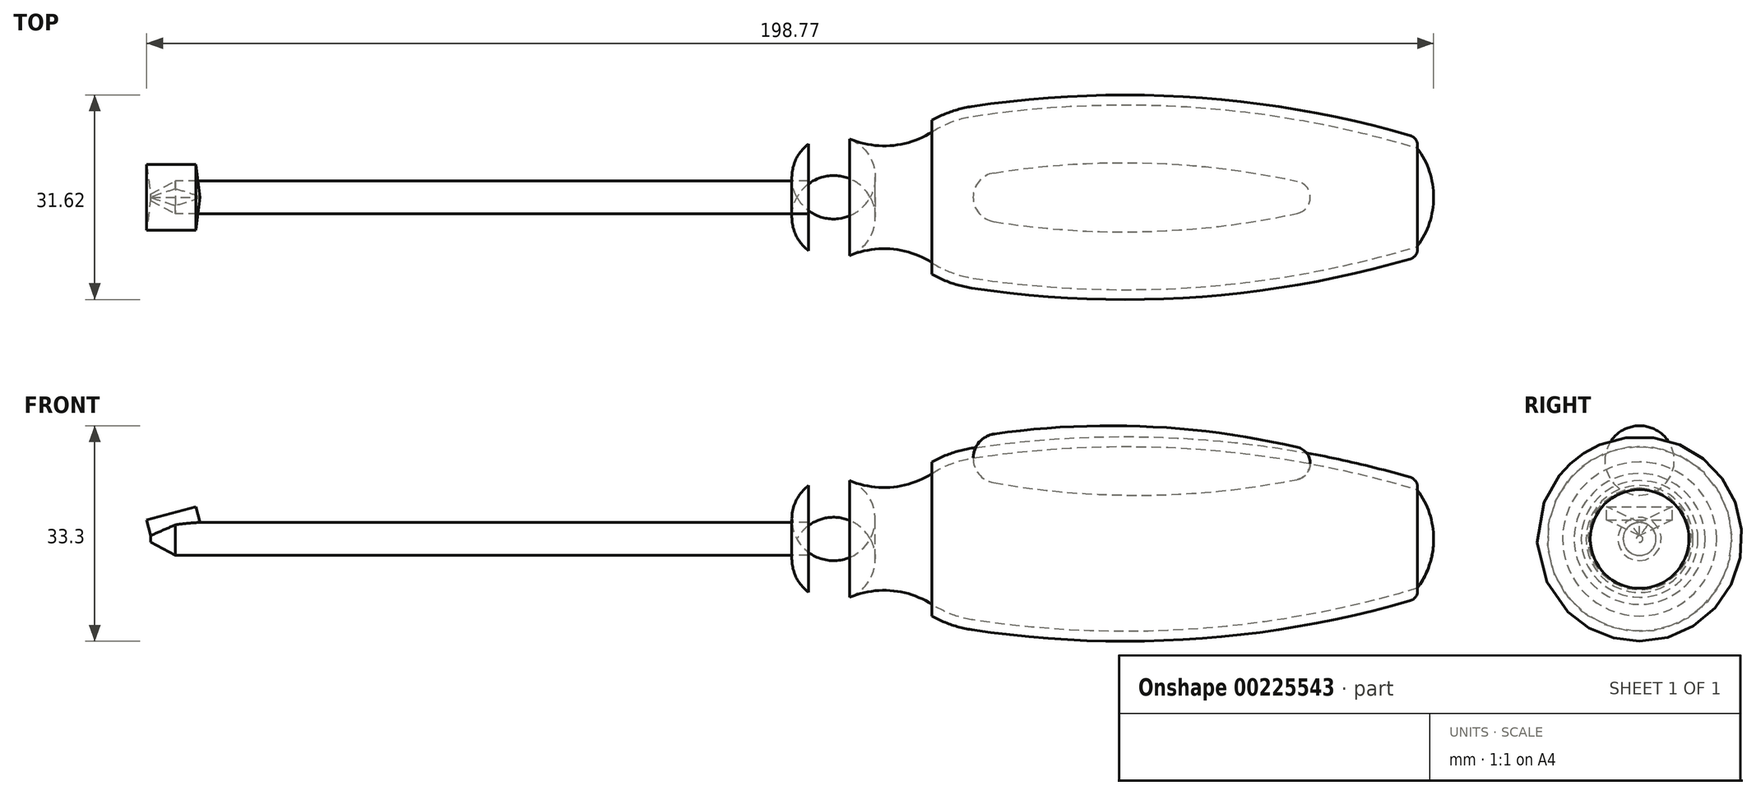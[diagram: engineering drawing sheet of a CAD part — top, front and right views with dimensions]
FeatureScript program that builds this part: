
annotation { "Feature Type Name" : "Feature", "Feature Type Description" : "" }
export const myFeature = defineFeature(function(context is Context, id is Id, definition is map)
    precondition{}
    {
        {
            var Q0;
            Q0=qCreatedBy(makeId("Front.planeOp"),FACE);
            var sketch = newSketch(context, id + "F0", { "sketchPlane" : qUnion([Q0])});
            skLineSegment(sketch, "E0", {"start": v(-101.6, 0) * mm, "end": v(96.52, 0) * mm});
            skLineSegment(sketch, "E1", {"start": v(96.52, 0) * mm, "end": v(117.55, 0) * mm, "construction": true});
            skLineSegment(sketch, "E2", {"start": v(50.8, 2.54) * mm, "end": v(-97.8, 2.54) * mm});
            skLineSegment(sketch, "E3", {"start": v(-101.6, 0.5) * mm, "end": v(-101.6, 0) * mm});
            skLineSegment(sketch, "E4", {"start": v(0, 2.54) * mm, "end": v(0, 8.25) * mm});
            skArc(sketch, "E5", {"start": v(6.35, 9.02) * mm, "mid": v(3.07, 9.48) * mm, "end": v(0, 8.25) * mm});
            skArc(sketch, "E6", {"start": v(6.35, 9.02) * mm, "mid": v(12.84, 7.99) * mm, "end": v(19.05, 10.11) * mm});
            skArc(sketch, "E7", {"start": v(25.4, 12.52) * mm, "mid": v(22.1, 11.65) * mm, "end": v(19.05, 10.11) * mm});
            skArc(sketch, "E8", {"start": v(93.98, 7.62) * mm, "mid": v(59.96, 13.9) * mm, "end": v(25.4, 12.52) * mm});
            skArc(sketch, "E9", {"start": v(96.52, 0) * mm, "mid": v(95.87, 4.02) * mm, "end": v(93.98, 7.62) * mm});
            skArc(sketch, "E10.0", {"start": v(25.17, 14.02) * mm, "mid": v(22.01, 13.24) * mm, "end": v(19.05, 11.9) * mm});
            skArc(sketch, "E10.1", {"start": v(92.95, 9.52) * mm, "mid": v(59.3, 15.46) * mm, "end": v(25.17, 14.02) * mm});
            skLineSegment(sketch, "E11", {"start": v(19.05, 11.9) * mm, "end": v(19.05, 10.11) * mm});
            skArc(sketch, "E12", {"start": v(93.98, 7.62) * mm, "mid": v(93.86, 8.78) * mm, "end": v(92.95, 9.52) * mm});
            skPoint(sketch, "E13.orphan", {"position": v(0, 0) * mm});
            skLineSegment(sketch, "E14", {"start": v(50.8, 2.54) * mm, "end": v(50.8, 0) * mm});
            skLineSegment(sketch, "E15", {"start": v(-101.6, 0.5) * mm, "end": v(-97.8, 2.54) * mm});
            skPoint(sketch, "E16.orphan", {"position": v(-101.6, 2.54) * mm});
            skSolve(sketch);
        }
        {
            var Q0;
            Q0=qCreatedBy(makeId("Front.planeOp"),FACE);
            var sketch = newSketch(context, id + "F1", { "sketchPlane" : qUnion([Q0])});
            skLineSegment(sketch, "E17", {"start": v(25.4, 12.52) * mm, "end": v(77.47, 11.64) * mm});
            skArc(sketch, "E18", {"start": v(28.67, 16.22) * mm, "mid": v(26.35, 14.97) * mm, "end": v(25.4, 12.52) * mm});
            skArc(sketch, "E19", {"start": v(77.47, 11.64) * mm, "mid": v(76.93, 13.25) * mm, "end": v(75.5, 14.16) * mm});
            skArc(sketch, "E20", {"start": v(75.5, 14.16) * mm, "mid": v(52.19, 17.37) * mm, "end": v(28.67, 16.22) * mm});
            skSolve(sketch);
        }
        {
            var Q0;
            Q0=qCreatedBy(makeId("Front.planeOp"),FACE);
            var sketch = newSketch(context, id + "F2", { "sketchPlane" : qUnion([Q0])});
            skLineSegment(sketch, "E21", {"start": v(-101.6, 0.5) * mm, "end": v(-93.98, 2.54) * mm});
            skSolve(sketch);
        }
        {
            var Q0;
            Q0=sQuery(id+"F2.wireOp",VERTEX,"E21.start");
            var Q1;
            Q1=sQuery(id+"F2.wireOp",EDGE,"E21");
            cPlane(context, id + "F3", {"entities" : qUnion([Q0, Q1]), "cplaneType" : CPlaneType.LINE_POINT, "offset" : 25.4 * mm, "width" : 152.4 * mm, "height" : 152.4 * mm});
        }
        {
            var Q0;
            Q0=qCreatedBy(id+"F3.planeOp",FACE);
            var sketch = newSketch(context, id + "F4", { "sketchPlane" : qUnion([Q0])});
            skLineSegment(sketch, "E22", {"start": v(5.08, 29.2) * mm, "end": v(0, 26.67) * mm});
            skLineSegment(sketch, "E23", {"start": v(0, 26.67) * mm, "end": v(-5.08, 29.2) * mm});
            skLineSegment(sketch, "E24", {"start": v(-5.08, 29.2) * mm, "end": v(5.08, 29.2) * mm});
            skLineSegment(sketch, "E25", {"start": v(0, 29.2) * mm, "end": v(0, 26.67) * mm, "construction": true});
            skSolve(sketch);
        }
        {
            var Q0;
            {var subQ0=sQuery(id+"F0.wireOp",EDGE,"E3");Q0=makeQuery(id+"F0.imprint","IMPRINT",FACE,{"disambiguationData":[TD([[makeQuery(id+"F0.imprint","IMPRINT",EDGE,{"derivedFrom":subQ0}),1.0]])]});}
            var Q1;
            {var subQ0=sQuery(id+"F0.wireOp",EDGE,"E4");Q1=makeQuery(id+"F0.imprint","IMPRINT",FACE,{"disambiguationData":[TD([[makeQuery(id+"F0.imprint","IMPRINT",EDGE,{"derivedFrom":subQ0}),-1.0]])]});}
            var Q2;
            Q2=sQuery(id+"F0.wireOp",EDGE,"E1");
            revolve(context, id + "F5", {"entities" : qUnion([Q0, Q1]), "axis" : qUnion([Q2]), "revolveType" : RevolveType.FULL});
        }
        {
            var Q0;
            Q0=makeQuery(id+"F4.imprint","IMPRINT",FACE,{"disambiguationData":[TD([[makeQuery(id+"F4.imprint","IMPRINT",EDGE,{"derivedFrom":sQuery(id+"F4.wireOp",EDGE,"E22")}),-1.0]])]});
            var Q1;
            Q1=sQuery(id+"F2.wireOp",EDGE,"E21");
            sweep(context, id + "F6", {"operationType" : NewBodyOperationType.REMOVE, "profiles" : qUnion([Q0]), "path" : qUnion([Q1])});
        }
        {
            var Q0;
            Q0=makeQuery(id+"F1.imprint","IMPRINT",FACE,{"disambiguationData":[TD([[makeQuery(id+"F1.imprint","IMPRINT",EDGE,{"derivedFrom":sQuery(id+"F1.wireOp",EDGE,"E17")}),1.0]])]});
            var Q1;
            Q1=sQuery(id+"F1.wireOp",EDGE,"E17");
            revolve(context, id + "F7", {"entities" : qUnion([Q0]), "axis" : qUnion([Q1]), "revolveType" : RevolveType.FULL});
        }
        {
            var Q0;
            Q0=makeQuery(id+"F0.imprint","IMPRINT",FACE,{"disambiguationData":[TD([[makeQuery(id+"F0.imprint","IMPRINT",EDGE,{"derivedFrom":sQuery(id+"F0.wireOp",EDGE,"E7")}),-1.0]])]});
            var Q1;
            Q1=makeQuery(id+"F5.opRevolve","SWEPT_FACE",FACE,{"disambiguationData":[OSD([sQuery(id+"F0.wireOp",EDGE,"E8")])]});
            revolve(context, id + "F8", {"entities" : qUnion([Q0]), "axis" : qUnion([Q1]), "revolveType" : RevolveType.FULL});
        }
        {
            var Q0;
            Q0=makeQuery(id+"F4.imprint","IMPRINT",FACE,{"disambiguationData":[TD([[makeQuery(id+"F4.imprint","IMPRINT",EDGE,{"derivedFrom":sQuery(id+"F4.wireOp",EDGE,"E22")}),-1.0]])]});
            var Q1;
            Q1=qConstructionFilter(qBodyType(qCreatedBy(id+"F2",EDGE),BodyType.WIRE),ConstructionObject.NO);
            sweep(context, id + "F9", {"profiles" : qUnion([Q0]), "path" : qUnion([Q1])});
        }
    });
